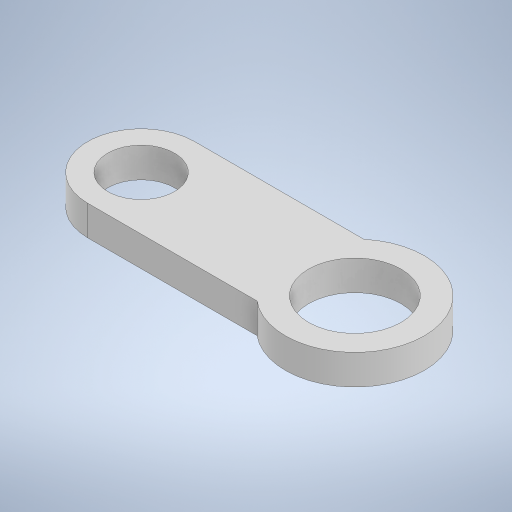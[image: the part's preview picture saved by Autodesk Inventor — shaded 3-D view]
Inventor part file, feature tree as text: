
AUTODESK INVENTOR PART (.ipt)
format: ipt  version: 2023 (Build 270158000, 158)  size: 239,616 bytes
history: native  units: in
note: dims shown in document units (in); Inventor stores cm internally (conversion verified against a paired STEP export)
features: extrude x1, sketch x1
ambient origin geometry x8: Origin, YZ Plane, XZ Plane, XY Plane, X Axis, Y Axis, Z Axis, Center Point
bodies: Solid1 (feature_tree)
feature tree (2):
  extrude  "Extrusion1"  Depth=0.281in TaperAngle=0.0deg
  sketch  "Sketch1"  dims[d4=0.625in d5=0.281in d6=0.0in d9=2.0in d3=0.5in]
